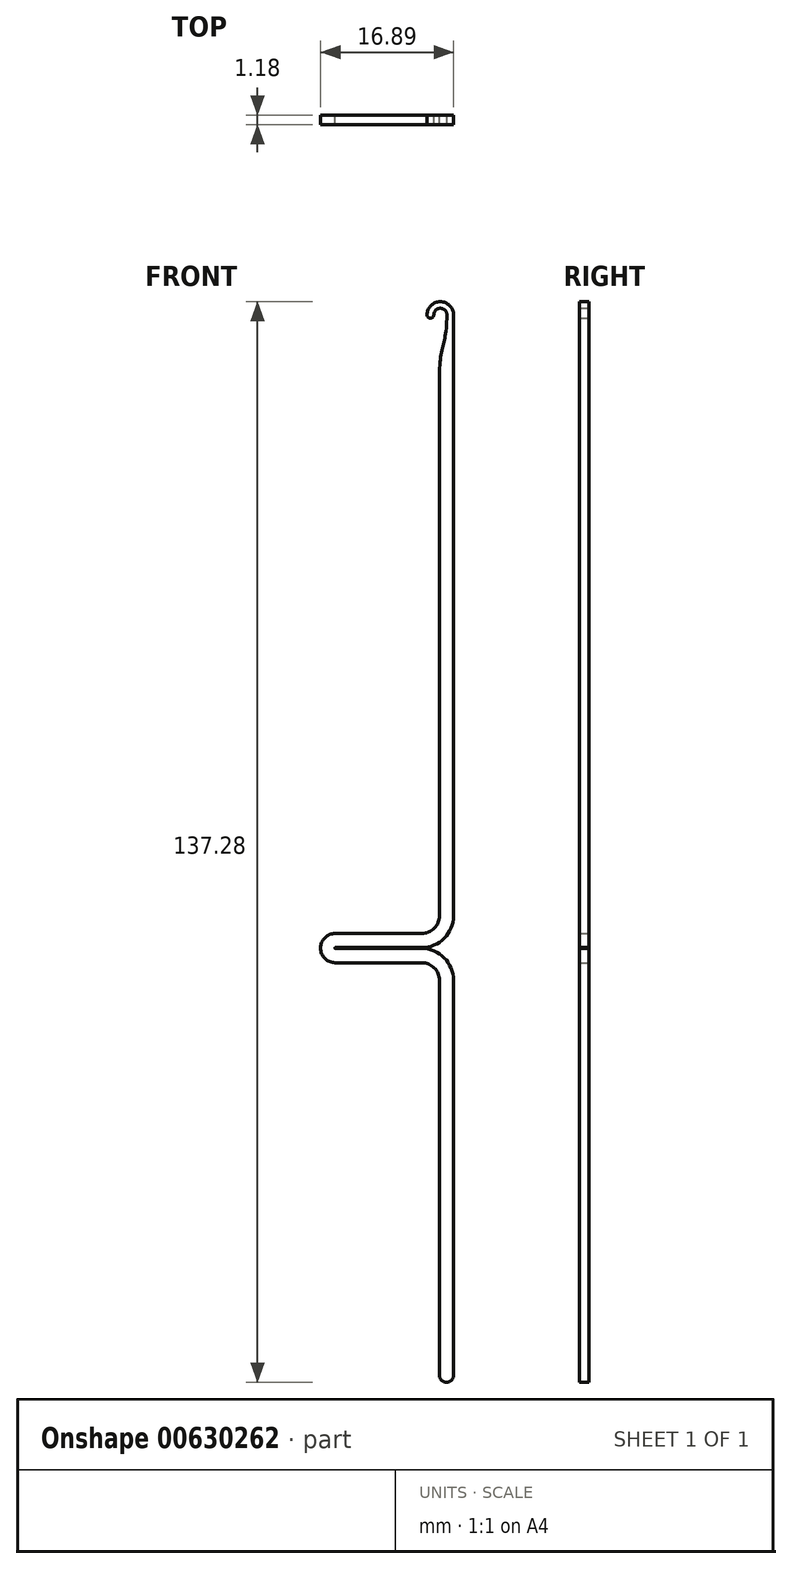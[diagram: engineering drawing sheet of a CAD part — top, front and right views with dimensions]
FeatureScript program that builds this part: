
annotation { "Feature Type Name" : "Feature", "Feature Type Description" : "" }
export const myFeature = defineFeature(function(context is Context, id is Id, definition is map)
    precondition{}
    {
        {
            var Q0;
            Q0=qCreatedBy(makeId("Front.planeOp"),FACE);
            var sketch = newSketch(context, id + "F0", { "sketchPlane" : qUnion([Q0])});
            skLineSegment(sketch, "E0", {"start": v(-0.9, 25.77) * mm, "end": v(-0.9, -127.89) * mm, "construction": true});
            skLineSegment(sketch, "E1", {"start": v(0.9, 16.45) * mm, "end": v(0.9, -127.89) * mm, "construction": true});
            skLineSegment(sketch, "E2", {"start": v(-0.9, 0) * mm, "end": v(0.9, 0) * mm, "construction": true});
            skLineSegment(sketch, "E3", {"start": v(-0.9, 0) * mm, "end": v(-0.9, -13.7) * mm});
            skLineSegment(sketch, "E4", {"start": v(0.9, 0) * mm, "end": v(0.9, -13.78) * mm});
            skLineSegment(sketch, "E5", {"start": v(-10.99, 0) * mm, "end": v(10.93, 0) * mm, "construction": true});
            skLineSegment(sketch, "E6", {"start": v(-12.12, 9.4) * mm, "end": v(16.1, 9.39) * mm, "construction": true});
            skLineSegment(sketch, "E7", {"start": v(-2.47, 13.72) * mm, "end": v(-2.47, -10.56) * mm, "construction": true});
            skLineSegment(sketch, "E8", {"start": v(-8.53, 7.7) * mm, "end": v(8.68, 7.7) * mm, "construction": true});
            skArc(sketch, "E9", {"start": v(0.9, 7.7) * mm, "mid": v(-0.78, 9.4) * mm, "end": v(-2.47, 7.7) * mm});
            skArc(sketch, "E10", {"start": v(0.05, 7.7) * mm, "mid": v(-0.78, 8.54) * mm, "end": v(-1.62, 7.7) * mm});
            skLineSegment(sketch, "E11", {"start": v(0.9, 0) * mm, "end": v(0.9, 7.7) * mm});
            skArc(sketch, "E12", {"start": v(-2.47, 7.7) * mm, "mid": v(-2.04, 7.28) * mm, "end": v(-1.62, 7.7) * mm});
            skFitSpline(sketch, "E13", {"points": [v(-0.9, 0) * mm, v(0.05, 7.7) * mm], "startDerivative": vector(0, 11.56) * mm, "endDerivative": vector(0, 11.56) * mm});
            skLineSegment(sketch, "E14", {"start": v(-0.9, 7.7) * mm, "end": v(-0.9, 0) * mm, "construction": true});
            skLineSegment(sketch, "E15", {"start": v(-8.02, -70.88) * mm, "end": v(9.61, -70.88) * mm, "construction": true});
            skLineSegment(sketch, "E16", {"start": v(-7.52, -74.6) * mm, "end": v(10.73, -74.6) * mm, "construction": true});
            skLineSegment(sketch, "E17", {"start": v(-7.05, -127.89) * mm, "end": v(10.82, -127.89) * mm, "construction": true});
            skLineSegment(sketch, "E18", {"start": v(-16, -59.92) * mm, "end": v(-16, -89.45) * mm, "construction": true});
            skArc(sketch, "E19", {"start": v(-14.14, -70.88) * mm, "mid": v(-16, -72.73) * mm, "end": v(-14.14, -74.59) * mm});
            skArc(sketch, "E20", {"start": v(-14.14, -72.68) * mm, "mid": v(-14.2, -72.73) * mm, "end": v(-14.13, -72.79) * mm});
            skArc(sketch, "E21", {"start": v(-3.15, -70.88) * mm, "mid": v(-1.56, -70.22) * mm, "end": v(-0.9, -68.63) * mm});
            skLineSegment(sketch, "E22", {"start": v(-14.14, -70.88) * mm, "end": v(-3.15, -70.88) * mm});
            skArc(sketch, "E23", {"start": v(-0.9, -76.84) * mm, "mid": v(-1.56, -75.25) * mm, "end": v(-3.15, -74.6) * mm});
            skLineSegment(sketch, "E24", {"start": v(-3.15, -74.59) * mm, "end": v(-14.14, -74.59) * mm});
            skArc(sketch, "E25", {"start": v(-0.9, -126.99) * mm, "mid": v(0, -127.89) * mm, "end": v(0.9, -126.99) * mm});
            skLineSegment(sketch, "E26", {"start": v(-0.9, -126.99) * mm, "end": v(-0.9, -76.84) * mm});
            skArc(sketch, "E27", {"start": v(0.9, -76.84) * mm, "mid": v(-0.29, -73.98) * mm, "end": v(-3.15, -72.8) * mm});
            skArc(sketch, "E28", {"start": v(-3.15, -72.68) * mm, "mid": v(-0.29, -71.5) * mm, "end": v(0.9, -68.63) * mm});
            skLineSegment(sketch, "E29", {"start": v(-14.14, -72.68) * mm, "end": v(-3.15, -72.68) * mm});
            skLineSegment(sketch, "E30", {"start": v(-3.15, -72.8) * mm, "end": v(-14.13, -72.79) * mm});
            skLineSegment(sketch, "E31", {"start": v(0.9, -76.84) * mm, "end": v(0.9, -126.99) * mm});
            skLineSegment(sketch, "E32", {"start": v(-0.9, -13.7) * mm, "end": v(-0.9, -68.63) * mm});
            skLineSegment(sketch, "E33", {"start": v(0.9, -68.63) * mm, "end": v(0.9, -13.78) * mm});
            skSolve(sketch);
        }
        {
            var Q0;
            Q0=makeQuery(id+"F0.imprint","IMPRINT",FACE,{"disambiguationData":[TD([[makeQuery(id+"F0.imprint","IMPRINT",EDGE,{"derivedFrom":sQuery(id+"F0.wireOp",EDGE,"E3")}),1.0]])]});
            extrude(context, id + "F1", {"entities" : qUnion([Q0]), "endBound" : BoundingType.SYMMETRIC, "depth" : 1.17 * mm, "offsetDistance" : 25 * mm});
        }
    });
